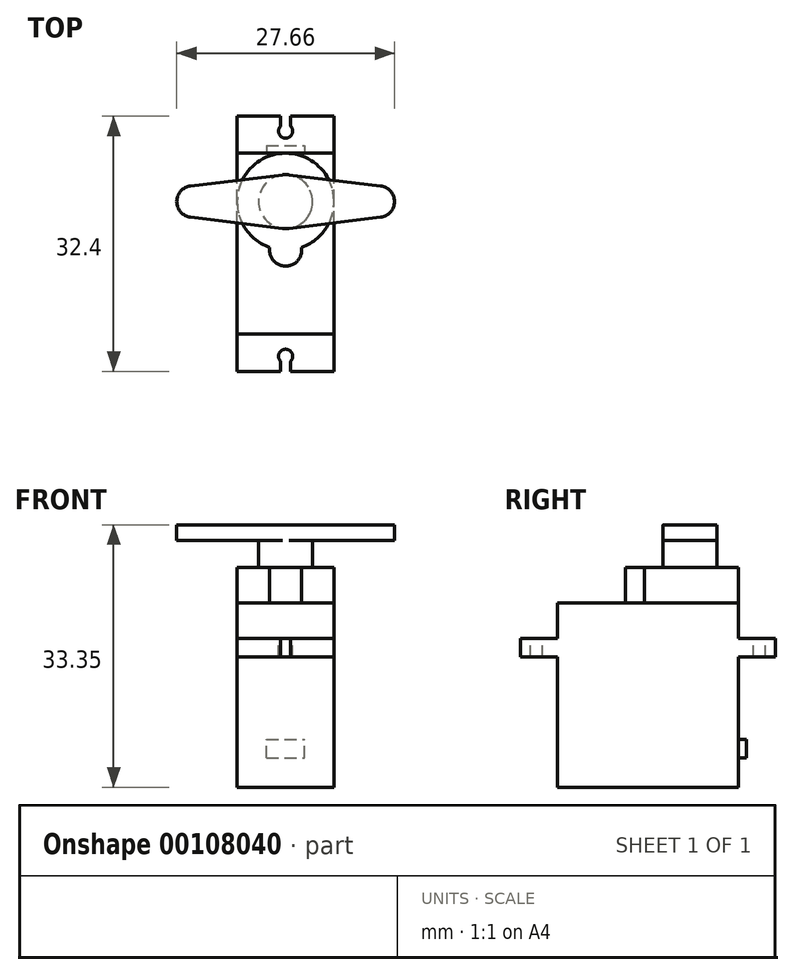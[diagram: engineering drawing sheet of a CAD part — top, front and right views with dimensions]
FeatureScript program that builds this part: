
annotation { "Feature Type Name" : "Feature", "Feature Type Description" : "" }
export const myFeature = defineFeature(function(context is Context, id is Id, definition is map)
    precondition{}
    {
        {
            var Q0;
            Q0=qCreatedBy(makeId("Front.planeOp"),FACE);
            var sketch = newSketch(context, id + "F0", { "sketchPlane" : qUnion([Q0])});
            skLineSegment(sketch, "E0.bottom", {"start": v(-6.15, 11.7) * mm, "end": v(6.15, 11.7) * mm});
            skLineSegment(sketch, "E0.top", {"start": v(-6.15, -11.7) * mm, "end": v(6.15, -11.7) * mm});
            skLineSegment(sketch, "E0.left", {"start": v(-6.15, 11.7) * mm, "end": v(-6.15, -11.7) * mm});
            skLineSegment(sketch, "E0.right", {"start": v(6.15, 11.7) * mm, "end": v(6.15, -11.7) * mm});
            skPoint(sketch, "E0.middle", {"position": v(0, 0) * mm});
            skSolve(sketch);
        }
        {
            var Q0;
            Q0 = qSketchRegion(id + "F0", true);
            extrude(context, id + "F1", {"entities" : qUnion([Q0]), "endBound" : BoundingType.SYMMETRIC, "depth" : 23 * mm});
        }
        {
            var Q0;
            Q0=makeQuery(id+"F1.opExtrude","SWEPT_FACE",FACE,{"disambiguationData":[OSD([sQuery(id+"F0.wireOp",EDGE,"E0.bottom")])]});
            cPlane(context, id + "F2", {"entities" : qUnion([Q0]), "cplaneType" : CPlaneType.OFFSET, "offset" : 4.5 * mm, "oppositeDirection" : true, "width" : 150 * mm, "height" : 150 * mm});
        }
        {
            var Q0;
            Q0=qCreatedBy(id+"F2.planeOp",FACE);
            var sketch = newSketch(context, id + "F3", { "sketchPlane" : qUnion([Q0])});
            skLineSegment(sketch, "E1", {"start": v(0, 0) * mm, "end": v(0, -11.5) * mm, "construction": true});
            skLineSegment(sketch, "E2.bottom", {"start": v(-6.15, -16.2) * mm, "end": v(-0.62, -16.2) * mm});
            skLineSegment(sketch, "E2.top", {"start": v(-6.15, -11.5) * mm, "end": v(6.15, -11.5) * mm});
            skLineSegment(sketch, "E2.left", {"start": v(-6.15, -16.2) * mm, "end": v(-6.15, -11.5) * mm});
            skLineSegment(sketch, "E2.right", {"start": v(6.15, -16.2) * mm, "end": v(6.15, -11.5) * mm});
            skLineSegment(sketch, "E3", {"start": v(0, 0) * mm, "end": v(9.38, 0) * mm, "construction": true});
            skArc(sketch, "E4", {"start": v(0.63, -14.95) * mm, "mid": v(0, -13.4) * mm, "end": v(-0.62, -14.95) * mm});
            skLineSegment(sketch, "E5", {"start": v(-0.62, -14.95) * mm, "end": v(-0.62, -16.2) * mm});
            skLineSegment(sketch, "E6.MirrorCS", {"start": v(0.63, -14.95) * mm, "end": v(0.63, -16.2) * mm});
            skLineSegment(sketch, "E7.trimOffspring", {"start": v(0.63, -16.2) * mm, "end": v(6.15, -16.2) * mm});
            skLineSegment(sketch, "E8.MirrorCS", {"start": v(-0.62, 14.95) * mm, "end": v(-0.62, 16.2) * mm});
            skLineSegment(sketch, "E9.MirrorCS", {"start": v(0.63, 14.95) * mm, "end": v(0.63, 16.2) * mm});
            skLineSegment(sketch, "E10.MirrorCS", {"start": v(-6.15, 11.5) * mm, "end": v(6.15, 11.5) * mm});
            skLineSegment(sketch, "E11.MirrorCS", {"start": v(-6.15, 16.2) * mm, "end": v(-6.15, 11.5) * mm});
            skLineSegment(sketch, "E12.MirrorCS", {"start": v(0.63, 16.2) * mm, "end": v(6.15, 16.2) * mm});
            skLineSegment(sketch, "E13.MirrorCS", {"start": v(6.15, 16.2) * mm, "end": v(6.15, 11.5) * mm});
            skLineSegment(sketch, "E14.MirrorCS", {"start": v(-6.15, 16.2) * mm, "end": v(-0.62, 16.2) * mm});
            skArc(sketch, "E15.MirrorCS", {"start": v(0.63, 14.95) * mm, "mid": v(0, 13.4) * mm, "end": v(-0.62, 14.95) * mm});
            skSolve(sketch);
        }
        {
            var Q0;
            Q0 = qSketchRegion(id + "F3", true);
            extrude(context, id + "F4", {"entities" : qUnion([Q0]), "operationType" : NewBodyOperationType.ADD, "oppositeDirection" : true, "depth" : 2.35 * mm});
        }
        {
            var Q0;
            {var subQ0=sQuery(id+"F0.wireOp",EDGE,"E0.right");var subQ1=sQuery(id+"F0.wireOp",EDGE,"E0.left");var subQ2=sQuery(id+"F0.wireOp",EDGE,"E0.top");Q0=makeQuery(id+"F4.boolean.opBoolean","SPLIT",FACE,{"disambiguationData":[TD([makeQuery(id+"F1.opExtrude","SWEPT_FACE",FACE,{"disambiguationData":[OSD([subQ2])]})])],"derivedFrom":makeQuery(id+"F1.opExtrude","CAP_FACE",FACE,{"disambiguationData":[OSD([sQuery(id+"F0.wireOp",EDGE,"E0.bottom"),subQ2,subQ1,subQ0])],"isStart":true})});}
            var sketch = newSketch(context, id + "F5", { "sketchPlane" : qUnion([Q0])});
            skLineSegment(sketch, "E16.bottom", {"start": v(2.42, -7.95) * mm, "end": v(-2.43, -7.95) * mm});
            skLineSegment(sketch, "E16.top", {"start": v(2.43, -5.6) * mm, "end": v(-2.42, -5.6) * mm});
            skLineSegment(sketch, "E16.left", {"start": v(2.42, -7.95) * mm, "end": v(2.43, -5.6) * mm});
            skLineSegment(sketch, "E16.right", {"start": v(-2.43, -7.95) * mm, "end": v(-2.42, -5.6) * mm});
            skPoint(sketch, "E16.middle", {"position": v(0, -6.77) * mm});
            skLineSegment(sketch, "E17", {"start": v(0, -6.77) * mm, "end": v(0, -11.7) * mm, "construction": true});
            skSolve(sketch);
        }
        {
            var Q0;
            Q0 = qSketchRegion(id + "F5", true);
            extrude(context, id + "F6", {"entities" : qUnion([Q0]), "operationType" : NewBodyOperationType.ADD, "depth" : 1 * mm});
        }
        {
            var Q0;
            Q0=makeQuery(id+"F1.opExtrude","SWEPT_FACE",FACE,{"disambiguationData":[OSD([sQuery(id+"F0.wireOp",EDGE,"E0.bottom")])]});
            var sketch = newSketch(context, id + "F7", { "sketchPlane" : qUnion([Q0])});
            skArc(sketch, "E18", {"start": v(2.02, -0.46) * mm, "mid": v(0, 11.5) * mm, "end": v(-2.02, -0.46) * mm});
            skArc(sketch, "E19", {"start": v(-2.02, -0.46) * mm, "mid": v(0, -2.85) * mm, "end": v(2.02, -0.46) * mm});
            skSolve(sketch);
        }
        {
            var Q0;
            Q0 = qSketchRegion(id + "F7", true);
            extrude(context, id + "F8", {"entities" : qUnion([Q0]), "operationType" : NewBodyOperationType.ADD, "depth" : 4.5 * mm});
        }
        {
            var Q0;
            Q0=makeQuery(id+"F8.opExtrude","CAP_FACE",FACE,{"disambiguationData":[OSD([sQuery(id+"F7.wireOp",EDGE,"E18"),sQuery(id+"F7.wireOp",EDGE,"E19")])],"isStart":false});
            var sketch = newSketch(context, id + "F9", { "sketchPlane" : qUnion([Q0])});
            skCircle(sketch, "E20", {"center": v(0, 5.35) * mm, "radius": 3.43 * mm});
            skSolve(sketch);
        }
        {
            var Q0;
            Q0 = qSketchRegion(id + "F9", true);
            extrude(context, id + "F10", {"entities" : qUnion([Q0]), "depth" : 5.45 * mm});
        }
        {
            var Q0;
            Q0=makeQuery(id+"F10.opExtrude","CAP_FACE",FACE,{"disambiguationData":[OSD([sQuery(id+"F9.wireOp",EDGE,"E20")])],"isStart":false});
            var sketch = newSketch(context, id + "F11", { "sketchPlane" : qUnion([Q0])});
            skLineSegment(sketch, "E21", {"start": v(0, 5.35) * mm, "end": v(-11.82, 5.35) * mm, "construction": true});
            skLineSegment(sketch, "E22", {"start": v(0, 5.35) * mm, "end": v(0, 0) * mm, "construction": true});
            skArc(sketch, "E23", {"start": v(-12.07, 7.34) * mm, "mid": v(-13.82, 5.35) * mm, "end": v(-12.07, 3.36) * mm});
            skArc(sketch, "E24.0", {"start": v(-0.41, 1.95) * mm, "mid": v(0, 1.93) * mm, "end": v(0.41, 1.95) * mm});
            skLineSegment(sketch, "E25", {"start": v(-0.41, 8.75) * mm, "end": v(-12.07, 7.34) * mm});
            skLineSegment(sketch, "E26.MirrorCS", {"start": v(-0.41, 1.95) * mm, "end": v(-12.07, 3.36) * mm});
            skLineSegment(sketch, "E27.MirrorCS", {"start": v(0.41, 1.95) * mm, "end": v(12.07, 3.36) * mm});
            skLineSegment(sketch, "E28.MirrorCS", {"start": v(0.41, 8.75) * mm, "end": v(12.07, 7.34) * mm});
            skArc(sketch, "E29.MirrorCS", {"start": v(12.07, 7.34) * mm, "mid": v(13.82, 5.35) * mm, "end": v(12.07, 3.36) * mm});
            skLineSegment(sketch, "E30", {"start": v(-11.82, 5.35) * mm, "end": v(-13.82, 5.35) * mm, "construction": true});
            skLineSegment(sketch, "E31", {"start": v(11.82, 5.35) * mm, "end": v(13.82, 5.35) * mm, "construction": true});
            skArc(sketch, "E32.trimOffspring", {"start": v(0.41, 8.75) * mm, "mid": v(0, 8.78) * mm, "end": v(-0.41, 8.75) * mm});
            skSolve(sketch);
        }
        {
            var Q0;
            Q0 = qSketchRegion(id + "F11", true);
            extrude(context, id + "F12", {"entities" : qUnion([Q0]), "operationType" : NewBodyOperationType.ADD, "oppositeDirection" : true, "depth" : 2 * mm});
        }
    });
